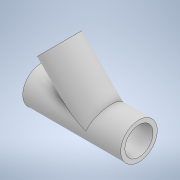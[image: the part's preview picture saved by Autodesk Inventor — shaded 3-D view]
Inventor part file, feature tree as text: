
AUTODESK INVENTOR PART (.ipt)
format: ipt  version: 2021.1 (Build 251245000, 245)  size: 154,112 bytes
history: native  units: in
note: dims shown in document units (in); Inventor stores cm internally (conversion verified against a paired STEP export)
features: extrude x2, sketch x2, other x1
ambient origin geometry x8: Origin, YZ Plane, XZ Plane, XY Plane, X Axis, Y Axis, Z Axis, Center Point
bodies: Solid1 (feature_tree)
feature tree (5):
  extrude  "Extrusion1"  TaperAngle=0.0deg  [1 undecoded]
  extrude  "Extrusion2"  Depth=0.1in
  sketch  "Sketch3"  dims[d0=1.0in d1=0.0in]
  sketch  "Sketch4"  dims[d2=0.515in d3=0.05in d4=0.515in d5=0.1in d6=0.0in]
  other  "Cut-Revolve2"
note: 1 required parameter value undecoded (feature->parameter linkage not recoverable at this tier; creation-order binding heuristic only, values carry confidence <= 0.55)
